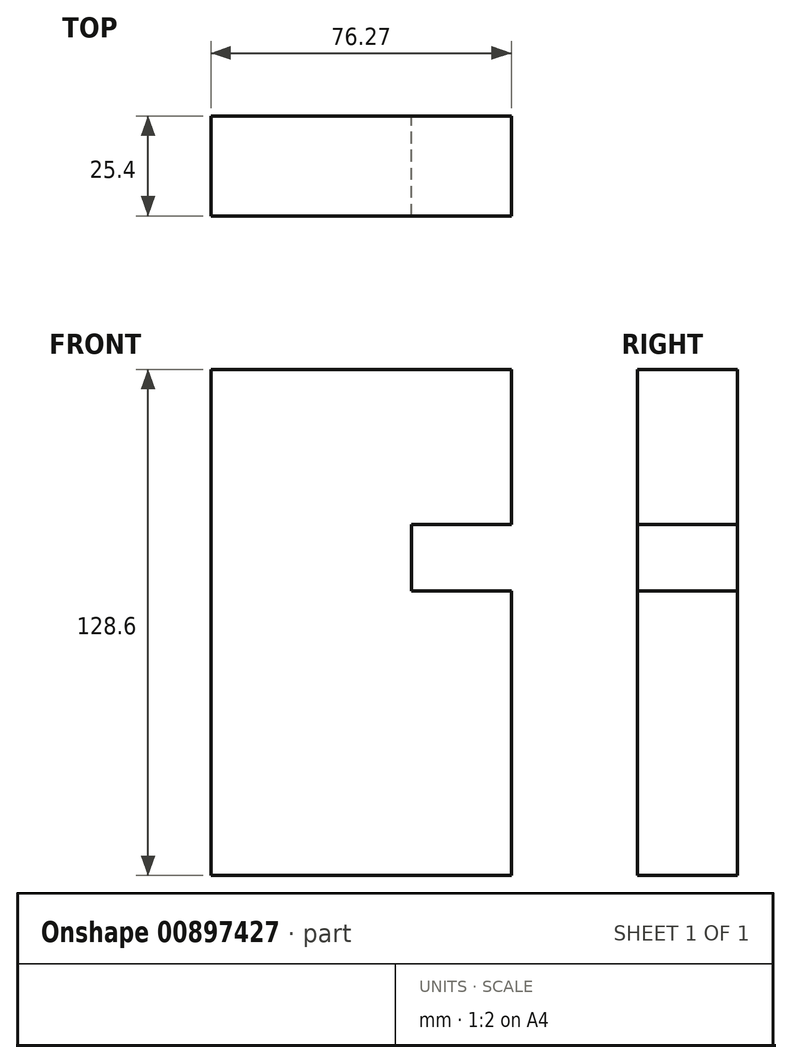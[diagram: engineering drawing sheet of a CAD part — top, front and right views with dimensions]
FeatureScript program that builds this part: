
annotation { "Feature Type Name" : "Feature", "Feature Type Description" : "" }
export const myFeature = defineFeature(function(context is Context, id is Id, definition is map)
    precondition{}
    {
        {
            var Q0;
            Q0=qCreatedBy(makeId("Front.planeOp"),FACE);
            var sketch = newSketch(context, id + "F0", { "sketchPlane" : qUnion([Q0])});
            skLineSegment(sketch, "E0.bottom", {"start": v(115, -56.78) * mm, "end": v(191.28, -56.78) * mm});
            skLineSegment(sketch, "E0.top", {"start": v(115, 71.82) * mm, "end": v(191.28, 71.82) * mm});
            skLineSegment(sketch, "E0.left", {"start": v(115, -56.78) * mm, "end": v(115, 71.82) * mm});
            skLineSegment(sketch, "E0.right", {"start": v(191.28, -56.78) * mm, "end": v(191.28, 71.82) * mm});
            skSolve(sketch);
        }
        {
            var Q0;
            Q0 = qSketchRegion(id + "F0", true);
            extrude(context, id + "F1", {"entities" : qUnion([Q0]), "depth" : 25.4 * mm, "offsetDistance" : 25.4 * mm});
        }
        {
            var Q0;
            Q0=makeQuery(id+"F1.opExtrude","SWEPT_FACE",FACE,{"disambiguationData":[OSD([sQuery(id+"F0.wireOp",EDGE,"E0.right")])]});
            var sketch = newSketch(context, id + "F2", { "sketchPlane" : qUnion([Q0])});
            skLineSegment(sketch, "E1", {"start": v(-25.4, 32.4) * mm, "end": v(0, 32.4) * mm});
            skLineSegment(sketch, "E2", {"start": v(-25.4, 15.58) * mm, "end": v(0, 15.58) * mm});
            skSolve(sketch);
        }
        {
            var Q0;
            {var subQ0=sQuery(id+"F2.wireOp",EDGE,"E1");Q0=makeQuery(id+"F2.imprint","IMPRINT",FACE,{"disambiguationData":[TD([[makeQuery(id+"F2.imprint","IMPRINT",EDGE,{"derivedFrom":subQ0}),-1.0]])]});}
            extrude(context, id + "F3", {"entities" : qUnion([Q0]), "operationType" : NewBodyOperationType.REMOVE, "oppositeDirection" : true, "depth" : 25.4 * mm, "offsetDistance" : 25.4 * mm});
        }
    });
